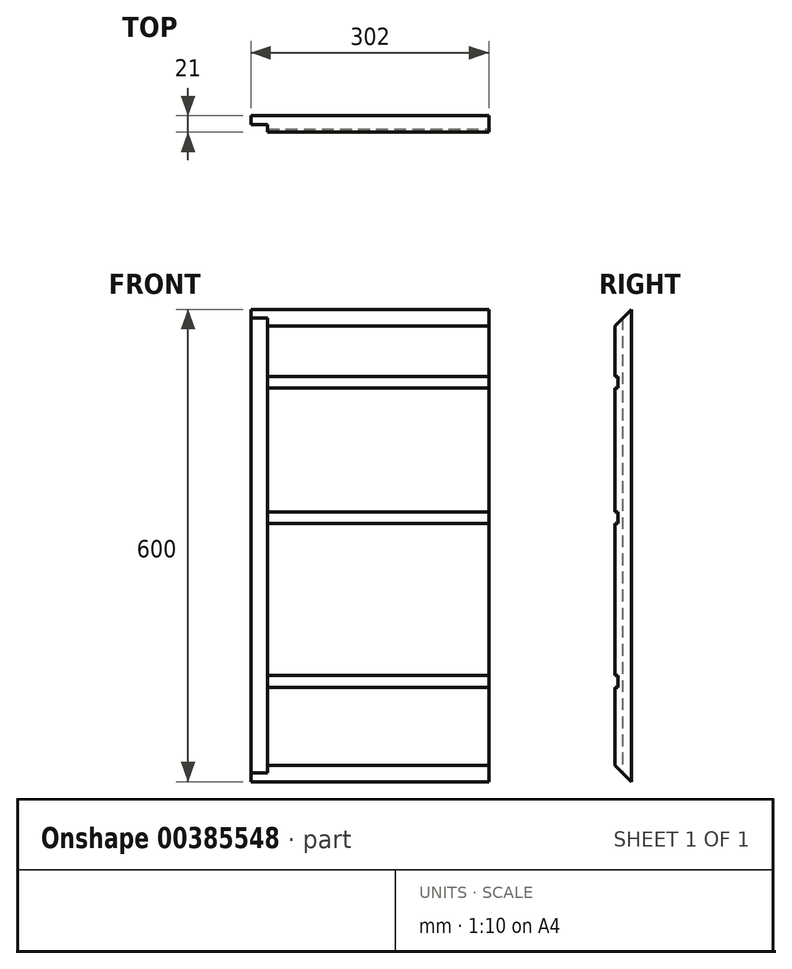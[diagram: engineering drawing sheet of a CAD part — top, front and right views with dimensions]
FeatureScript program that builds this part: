
annotation { "Feature Type Name" : "Feature", "Feature Type Description" : "" }
export const myFeature = defineFeature(function(context is Context, id is Id, definition is map)
    precondition{}
    {
        {
            var Q0;
            Q0=qCreatedBy(makeId("Front.planeOp"),FACE);
            var sketch = newSketch(context, id + "F0", { "sketchPlane" : qUnion([Q0])});
            skLineSegment(sketch, "E0.bottom", {"start": v(0, 600) * mm, "end": v(302, 600) * mm});
            skLineSegment(sketch, "E0.top", {"start": v(0, 0) * mm, "end": v(302, 0) * mm});
            skLineSegment(sketch, "E0.left", {"start": v(0, 600) * mm, "end": v(0, 0) * mm});
            skLineSegment(sketch, "E0.right", {"start": v(302, 600) * mm, "end": v(302, 0) * mm});
            skSolve(sketch);
        }
        {
            var Q0;
            Q0=makeQuery(id+"F0.imprint","IMPRINT",FACE,{"disambiguationData":[TD([[makeQuery(id+"F0.imprint","IMPRINT",EDGE,{"derivedFrom":sQuery(id+"F0.wireOp",EDGE,"E0.bottom")}),-1.0]])]});
            extrude(context, id + "F1", {"entities" : qUnion([Q0]), "oppositeDirection" : true, "depth" : 21 * mm});
        }
        {
            var Q0;
            Q0=makeQuery(id+"F1.opExtrude","CAP_EDGE",EDGE,{"disambiguationData":[OSD([sQuery(id+"F0.wireOp",EDGE,"E0.top")])],"isStart":true});
            var Q1;
            Q1=makeQuery(id+"F1.opExtrude","CAP_EDGE",EDGE,{"disambiguationData":[OSD([sQuery(id+"F0.wireOp",EDGE,"E0.bottom")])],"isStart":true});
            chamfer(context, id + "F2", {"entities" : qUnion([Q0, Q1]), "width" : 21 * mm, "tangentPropagation" : true});
        }
        {
            var Q0;
            Q0=makeQuery(id+"F1.opExtrude","CAP_FACE",FACE,{"disambiguationData":[OSD([sQuery(id+"F0.wireOp",EDGE,"E0.bottom"),sQuery(id+"F0.wireOp",EDGE,"E0.top"),sQuery(id+"F0.wireOp",EDGE,"E0.left"),sQuery(id+"F0.wireOp",EDGE,"E0.right")])],"isStart":true});
            var sketch = newSketch(context, id + "F3", { "sketchPlane" : qUnion([Q0])});
            skLineSegment(sketch, "E1.bottom", {"start": v(0, 600) * mm, "end": v(21, 600) * mm});
            skLineSegment(sketch, "E1.top", {"start": v(0, 0) * mm, "end": v(21, 0) * mm});
            skLineSegment(sketch, "E1.left", {"start": v(0, 600) * mm, "end": v(0, 0) * mm});
            skLineSegment(sketch, "E1.right", {"start": v(21, 600) * mm, "end": v(21, 0) * mm});
            skSolve(sketch);
        }
        {
            var Q0;
            Q0 = qSketchRegion(id + "F3", true);
            extrude(context, id + "F4", {"entities" : qUnion([Q0]), "operationType" : NewBodyOperationType.REMOVE, "oppositeDirection" : true, "depth" : 10 * mm});
        }
        {
            var Q0;
            Q0=makeQuery(id+"F1.opExtrude","CAP_FACE",FACE,{"disambiguationData":[OSD([sQuery(id+"F0.wireOp",EDGE,"E0.bottom"),sQuery(id+"F0.wireOp",EDGE,"E0.top"),sQuery(id+"F0.wireOp",EDGE,"E0.left"),sQuery(id+"F0.wireOp",EDGE,"E0.right")])],"isStart":true});
            var sketch = newSketch(context, id + "F5", { "sketchPlane" : qUnion([Q0])});
            skLineSegment(sketch, "E2.0", {"start": v(0, 515) * mm, "end": v(302, 515) * mm});
            skLineSegment(sketch, "E3", {"start": v(0, 515) * mm, "end": v(0, 500) * mm});
            skLineSegment(sketch, "E4", {"start": v(0, 500) * mm, "end": v(302, 500) * mm});
            skLineSegment(sketch, "E5", {"start": v(302, 500) * mm, "end": v(302, 515) * mm});
            skSolve(sketch);
        }
        {
            var Q0;
            Q0 = qSketchRegion(id + "F5", true);
            extrude(context, id + "F6", {"entities" : qUnion([Q0]), "operationType" : NewBodyOperationType.REMOVE, "oppositeDirection" : true, "depth" : 4 * mm});
        }
        {
            var Q0;
            {var subQ0=sQuery(id+"F0.wireOp",EDGE,"E0.right");var subQ1=sQuery(id+"F0.wireOp",EDGE,"E0.top");Q0=makeQuery(id+"F6.boolean.opBoolean","SPLIT",FACE,{"disambiguationData":[TD([makeQuery(id+"F2.opChamfer","BLEND_FACE",FACE,{"disambiguationData":[OSD([subQ1])]})])],"derivedFrom":makeQuery(id+"F1.opExtrude","CAP_FACE",FACE,{"disambiguationData":[OSD([sQuery(id+"F0.wireOp",EDGE,"E0.bottom"),subQ1,sQuery(id+"F0.wireOp",EDGE,"E0.left"),subQ0])],"isStart":true})});}
            var sketch = newSketch(context, id + "F7", { "sketchPlane" : qUnion([Q0])});
            skLineSegment(sketch, "E6.bottom", {"start": v(21, 343) * mm, "end": v(302, 343) * mm});
            skLineSegment(sketch, "E6.top", {"start": v(21, 328) * mm, "end": v(302, 328) * mm});
            skLineSegment(sketch, "E6.left", {"start": v(21, 343) * mm, "end": v(21, 328) * mm});
            skLineSegment(sketch, "E6.right", {"start": v(302, 343) * mm, "end": v(302, 328) * mm});
            skLineSegment(sketch, "E7.bottom", {"start": v(21, 135) * mm, "end": v(302, 135) * mm});
            skLineSegment(sketch, "E7.top", {"start": v(21, 120) * mm, "end": v(302, 120) * mm});
            skLineSegment(sketch, "E7.left", {"start": v(21, 135) * mm, "end": v(21, 120) * mm});
            skLineSegment(sketch, "E7.right", {"start": v(302, 135) * mm, "end": v(302, 120) * mm});
            skSolve(sketch);
        }
        {
            var Q0;
            Q0 = qSketchRegion(id + "F7", true);
            extrude(context, id + "F8", {"entities" : qUnion([Q0]), "operationType" : NewBodyOperationType.REMOVE, "oppositeDirection" : true, "depth" : 4 * mm});
        }
    });
